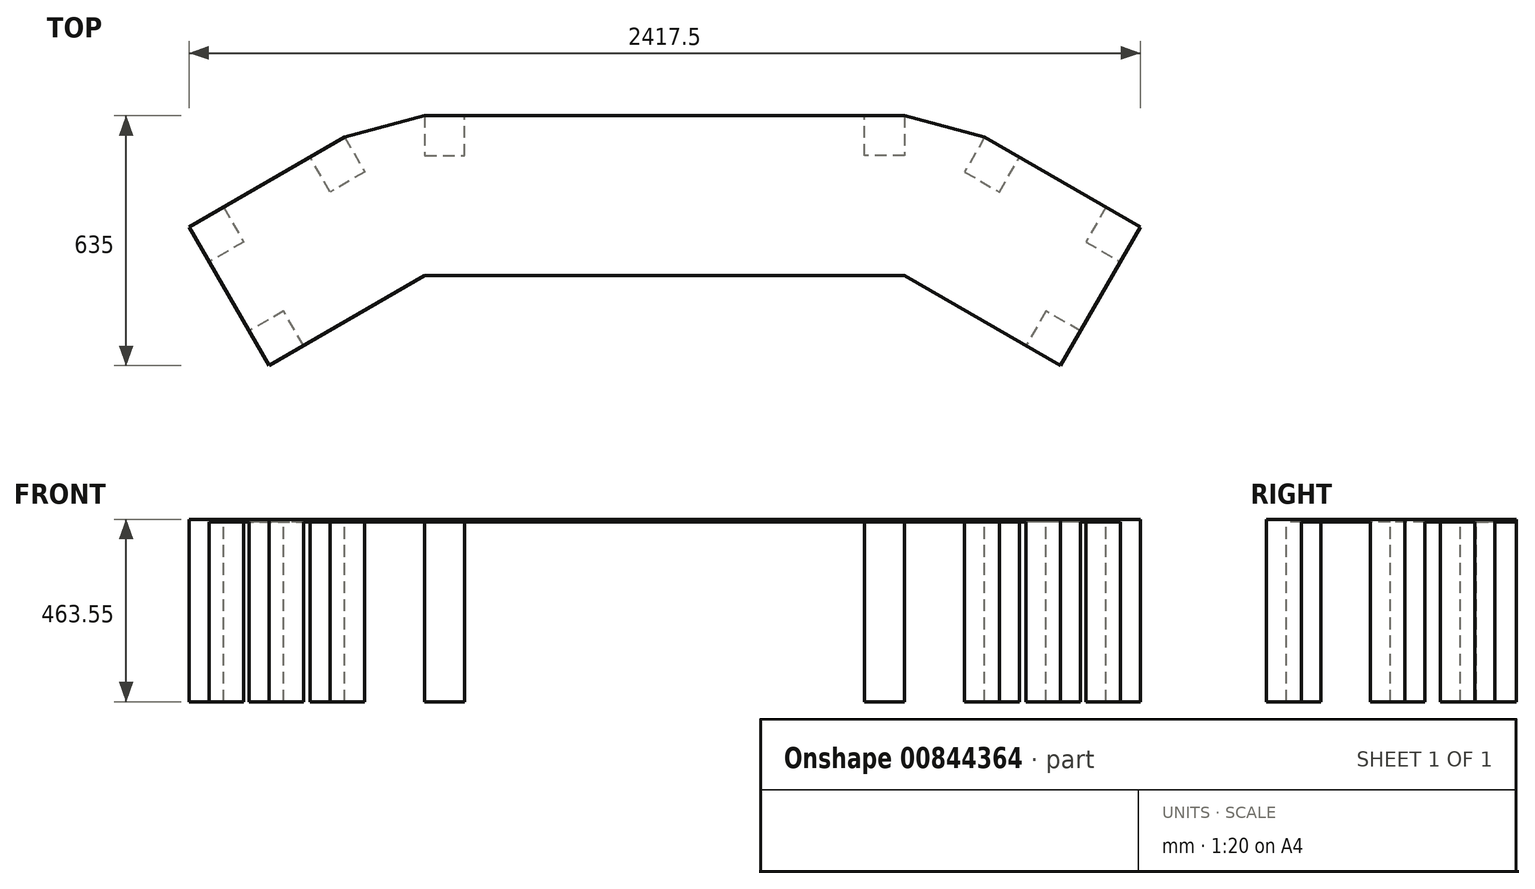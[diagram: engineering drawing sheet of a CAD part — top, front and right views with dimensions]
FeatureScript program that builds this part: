
annotation { "Feature Type Name" : "Feature", "Feature Type Description" : "" }
export const myFeature = defineFeature(function(context is Context, id is Id, definition is map)
    precondition{}
    {
        {
            var Q0;
            Q0=qCreatedBy(makeId("Top.planeOp"),FACE);
            var sketch = newSketch(context, id + "F0", { "sketchPlane" : qUnion([Q0])});
            skLineSegment(sketch, "E0.bottom", {"start": v(609.6, 203.2) * mm, "end": v(-609.6, 203.2) * mm});
            skLineSegment(sketch, "E0.top", {"start": v(609.6, -203.2) * mm, "end": v(-609.6, -203.2) * mm});
            skLineSegment(sketch, "E0.left", {"start": v(609.6, 203.2) * mm, "end": v(609.6, -203.2) * mm});
            skLineSegment(sketch, "E0.right", {"start": v(-609.6, 203.2) * mm, "end": v(-609.6, -203.2) * mm});
            skPoint(sketch, "E0.middle", {"position": v(0, 0) * mm});
            skLineSegment(sketch, "E1", {"start": v(-609.6, -203.2) * mm, "end": v(-1005.55, -431.8) * mm});
            skLineSegment(sketch, "E2", {"start": v(-1005.55, -431.8) * mm, "end": v(-1208.75, -79.85) * mm});
            skLineSegment(sketch, "E3", {"start": v(-1208.75, -79.85) * mm, "end": v(-812.8, 148.75) * mm});
            skLineSegment(sketch, "E4", {"start": v(-812.8, 148.75) * mm, "end": v(-609.6, -203.2) * mm});
            skLineSegment(sketch, "E5", {"start": v(-609.6, 203.2) * mm, "end": v(-812.8, 148.75) * mm});
            skLineSegment(sketch, "E6", {"start": v(609.6, -203.2) * mm, "end": v(1005.55, -431.8) * mm});
            skLineSegment(sketch, "E7", {"start": v(1005.55, -431.8) * mm, "end": v(1208.75, -79.85) * mm});
            skLineSegment(sketch, "E8", {"start": v(1208.75, -79.85) * mm, "end": v(812.8, 148.75) * mm});
            skLineSegment(sketch, "E9", {"start": v(812.8, 148.75) * mm, "end": v(609.6, -203.2) * mm});
            skLineSegment(sketch, "E10", {"start": v(609.6, 203.2) * mm, "end": v(812.8, 148.75) * mm});
            skSolve(sketch);
        }
        {
            var Q0;
            Q0=makeQuery(id+"F0.imprint","IMPRINT",FACE,{"disambiguationData":[TD([[makeQuery(id+"F0.imprint","IMPRINT",EDGE,{"derivedFrom":sQuery(id+"F0.wireOp",EDGE,"E6")}),1.0]])]});
            var Q1;
            Q1=makeQuery(id+"F0.imprint","IMPRINT",FACE,{"disambiguationData":[TD([[makeQuery(id+"F0.imprint","IMPRINT",EDGE,{"derivedFrom":sQuery(id+"F0.wireOp",EDGE,"E0.left")}),1.0]])]});
            var Q2;
            Q2=makeQuery(id+"F0.imprint","IMPRINT",FACE,{"disambiguationData":[TD([[makeQuery(id+"F0.imprint","IMPRINT",EDGE,{"derivedFrom":sQuery(id+"F0.wireOp",EDGE,"E0.bottom")}),1.0]])]});
            var Q3;
            Q3=makeQuery(id+"F0.imprint","IMPRINT",FACE,{"disambiguationData":[TD([[makeQuery(id+"F0.imprint","IMPRINT",EDGE,{"derivedFrom":sQuery(id+"F0.wireOp",EDGE,"E0.right")}),-1.0]])]});
            var Q4;
            Q4=makeQuery(id+"F0.imprint","IMPRINT",FACE,{"disambiguationData":[TD([[makeQuery(id+"F0.imprint","IMPRINT",EDGE,{"derivedFrom":sQuery(id+"F0.wireOp",EDGE,"E1")}),-1.0]])]});
            extrude(context, id + "F1", {"entities" : qUnion([Q0, Q1, Q2, Q3, Q4]), "depth" : 6.35 * mm, "offsetDistance" : 25.4 * mm});
        }
        {
            var Q0;
            Q0=makeQuery(id+"F1.opExtrude","CAP_FACE",FACE,{"disambiguationData":[OSD([sQuery(id+"F0.wireOp",EDGE,"E0.bottom"),sQuery(id+"F0.wireOp",EDGE,"E0.top"),sQuery(id+"F0.wireOp",EDGE,"E1"),sQuery(id+"F0.wireOp",EDGE,"E2"),sQuery(id+"F0.wireOp",EDGE,"E3"),sQuery(id+"F0.wireOp",EDGE,"E5"),sQuery(id+"F0.wireOp",EDGE,"E6"),sQuery(id+"F0.wireOp",EDGE,"E7"),sQuery(id+"F0.wireOp",EDGE,"E8"),sQuery(id+"F0.wireOp",EDGE,"E10")])],"isStart":true});
            var sketch = newSketch(context, id + "F2", { "sketchPlane" : qUnion([Q0])});
            skLineSegment(sketch, "E11", {"start": v(1208.75, 79.85) * mm, "end": v(1120.76, 29.05) * mm});
            skLineSegment(sketch, "E12", {"start": v(1120.76, 29.05) * mm, "end": v(1069.96, 117.04) * mm});
            skLineSegment(sketch, "E13", {"start": v(1069.96, 117.04) * mm, "end": v(1157.95, 167.84) * mm});
            skLineSegment(sketch, "E14", {"start": v(1157.95, 167.84) * mm, "end": v(1208.75, 79.85) * mm});
            skLineSegment(sketch, "E15", {"start": v(1005.55, 431.8) * mm, "end": v(1056.35, 343.81) * mm});
            skLineSegment(sketch, "E16", {"start": v(1056.35, 343.81) * mm, "end": v(968.36, 293.01) * mm});
            skLineSegment(sketch, "E17", {"start": v(968.36, 293.01) * mm, "end": v(917.56, 381) * mm});
            skLineSegment(sketch, "E18", {"start": v(917.56, 381) * mm, "end": v(1005.55, 431.8) * mm});
            skLineSegment(sketch, "E19", {"start": v(812.8, -148.75) * mm, "end": v(762, -60.76) * mm});
            skLineSegment(sketch, "E20", {"start": v(762, -60.76) * mm, "end": v(849.99, -9.96) * mm});
            skLineSegment(sketch, "E21", {"start": v(849.99, -9.96) * mm, "end": v(900.79, -97.95) * mm});
            skLineSegment(sketch, "E22", {"start": v(900.79, -97.95) * mm, "end": v(812.8, -148.75) * mm});
            skLineSegment(sketch, "E23", {"start": v(609.6, 203.2) * mm, "end": v(660.4, 115.21) * mm});
            skLineSegment(sketch, "E24", {"start": v(660.4, 115.21) * mm, "end": v(748.39, 166.01) * mm});
            skLineSegment(sketch, "E25", {"start": v(748.39, 166.01) * mm, "end": v(697.59, 254) * mm});
            skLineSegment(sketch, "E26", {"start": v(697.59, 254) * mm, "end": v(609.6, 203.2) * mm});
            skLineSegment(sketch, "E27", {"start": v(-1208.75, 79.85) * mm, "end": v(-1120.76, 29.05) * mm});
            skLineSegment(sketch, "E28", {"start": v(-1120.76, 29.05) * mm, "end": v(-1069.96, 117.04) * mm});
            skLineSegment(sketch, "E29", {"start": v(-1069.96, 117.04) * mm, "end": v(-1157.95, 167.84) * mm});
            skLineSegment(sketch, "E30", {"start": v(-1157.95, 167.84) * mm, "end": v(-1208.75, 79.85) * mm});
            skLineSegment(sketch, "E31", {"start": v(-1005.55, 431.8) * mm, "end": v(-917.56, 381) * mm});
            skLineSegment(sketch, "E32", {"start": v(-917.56, 381) * mm, "end": v(-968.36, 293.01) * mm});
            skLineSegment(sketch, "E33", {"start": v(-968.36, 293.01) * mm, "end": v(-1056.35, 343.81) * mm});
            skLineSegment(sketch, "E34", {"start": v(-1056.35, 343.81) * mm, "end": v(-1005.55, 431.8) * mm});
            skLineSegment(sketch, "E35", {"start": v(-609.6, 203.2) * mm, "end": v(-697.59, 254) * mm});
            skLineSegment(sketch, "E36", {"start": v(-697.59, 254) * mm, "end": v(-748.39, 166.01) * mm});
            skLineSegment(sketch, "E37", {"start": v(-748.39, 166.01) * mm, "end": v(-660.4, 115.21) * mm});
            skLineSegment(sketch, "E38", {"start": v(-660.4, 115.21) * mm, "end": v(-609.6, 203.2) * mm});
            skLineSegment(sketch, "E39", {"start": v(-812.8, -148.75) * mm, "end": v(-762, -60.76) * mm});
            skLineSegment(sketch, "E40", {"start": v(-762, -60.76) * mm, "end": v(-849.99, -9.96) * mm});
            skLineSegment(sketch, "E41", {"start": v(-849.99, -9.96) * mm, "end": v(-900.79, -97.95) * mm});
            skLineSegment(sketch, "E42", {"start": v(849.99, -9.96) * mm, "end": v(1069.96, 117.04) * mm});
            skLineSegment(sketch, "E43", {"start": v(968.36, 293.01) * mm, "end": v(1069.96, 117.04) * mm});
            skLineSegment(sketch, "E44", {"start": v(849.99, -9.96) * mm, "end": v(748.39, 166.01) * mm});
            skLineSegment(sketch, "E45", {"start": v(968.36, 293.01) * mm, "end": v(748.39, 166.01) * mm});
            skLineSegment(sketch, "E46", {"start": v(1120.76, 29.05) * mm, "end": v(900.79, -97.95) * mm});
            skLineSegment(sketch, "E47", {"start": v(762, -60.76) * mm, "end": v(660.4, 115.21) * mm});
            skLineSegment(sketch, "E48", {"start": v(697.59, 254) * mm, "end": v(917.56, 381) * mm});
            skLineSegment(sketch, "E49", {"start": v(1056.35, 343.81) * mm, "end": v(1157.95, 167.84) * mm});
            skLineSegment(sketch, "E50", {"start": v(-917.56, 381) * mm, "end": v(-697.59, 254) * mm});
            skLineSegment(sketch, "E51", {"start": v(-660.4, 115.21) * mm, "end": v(-762, -60.76) * mm});
            skLineSegment(sketch, "E52", {"start": v(-849.99, -9.96) * mm, "end": v(-1069.96, 117.04) * mm});
            skLineSegment(sketch, "E53", {"start": v(-968.36, 293.01) * mm, "end": v(-748.39, 166.01) * mm});
            skLineSegment(sketch, "E54", {"start": v(-968.36, 293.01) * mm, "end": v(-1069.96, 117.04) * mm});
            skLineSegment(sketch, "E55", {"start": v(-1056.35, 343.81) * mm, "end": v(-1157.95, 167.84) * mm});
            skLineSegment(sketch, "E56", {"start": v(-900.79, -97.95) * mm, "end": v(-1120.76, 29.05) * mm});
            skLineSegment(sketch, "E57", {"start": v(-748.39, 166.01) * mm, "end": v(-849.99, -9.96) * mm});
            skLineSegment(sketch, "E58", {"start": v(-609.6, 203.2) * mm, "end": v(-609.6, 101.6) * mm});
            skLineSegment(sketch, "E59", {"start": v(-609.6, 101.6) * mm, "end": v(-508, 101.6) * mm});
            skLineSegment(sketch, "E60", {"start": v(-508, 101.6) * mm, "end": v(-508, 203.2) * mm});
            skLineSegment(sketch, "E61", {"start": v(-508, 203.2) * mm, "end": v(-609.6, 203.2) * mm});
            skLineSegment(sketch, "E62", {"start": v(-609.6, -203.2) * mm, "end": v(-609.6, -101.6) * mm});
            skLineSegment(sketch, "E63", {"start": v(-609.6, -101.6) * mm, "end": v(-508, -101.6) * mm});
            skLineSegment(sketch, "E64", {"start": v(-508, -101.6) * mm, "end": v(-508, -203.2) * mm});
            skLineSegment(sketch, "E65", {"start": v(-508, -203.2) * mm, "end": v(-609.6, -203.2) * mm});
            skLineSegment(sketch, "E66", {"start": v(609.6, 203.2) * mm, "end": v(508, 203.2) * mm});
            skLineSegment(sketch, "E67", {"start": v(508, 203.2) * mm, "end": v(508, 101.6) * mm});
            skLineSegment(sketch, "E68", {"start": v(508, 101.6) * mm, "end": v(609.6, 101.6) * mm});
            skLineSegment(sketch, "E69", {"start": v(609.6, 101.6) * mm, "end": v(609.6, 203.2) * mm});
            skLineSegment(sketch, "E70", {"start": v(609.6, -203.2) * mm, "end": v(609.6, -101.6) * mm});
            skLineSegment(sketch, "E71", {"start": v(609.6, -101.6) * mm, "end": v(508, -101.6) * mm});
            skLineSegment(sketch, "E72", {"start": v(508, -101.6) * mm, "end": v(508, -203.2) * mm});
            skLineSegment(sketch, "E73", {"start": v(508, -203.2) * mm, "end": v(609.6, -203.2) * mm});
            skLineSegment(sketch, "E74", {"start": v(-508, 203.2) * mm, "end": v(508, 203.2) * mm});
            skLineSegment(sketch, "E75", {"start": v(609.6, 101.6) * mm, "end": v(609.6, -101.6) * mm});
            skLineSegment(sketch, "E76", {"start": v(508, -101.6) * mm, "end": v(508, 101.6) * mm});
            skLineSegment(sketch, "E77", {"start": v(-508, 101.6) * mm, "end": v(508, 101.6) * mm});
            skLineSegment(sketch, "E78", {"start": v(508, -101.6) * mm, "end": v(-508, -101.6) * mm});
            skLineSegment(sketch, "E79", {"start": v(-508, -203.2) * mm, "end": v(508, -203.2) * mm});
            skLineSegment(sketch, "E80", {"start": v(-508, 101.6) * mm, "end": v(-508, -101.6) * mm});
            skLineSegment(sketch, "E81", {"start": v(-609.6, -101.6) * mm, "end": v(-609.6, 101.6) * mm});
            skSolve(sketch);
        }
        {
            var Q0;
            Q0=makeQuery(id+"F2.imprint","IMPRINT",FACE,{"disambiguationData":[TD([[makeQuery(id+"F2.imprint","IMPRINT",EDGE,{"derivedFrom":sQuery(id+"F2.wireOp",EDGE,"E31")}),1.0]])]});
            var Q1;
            Q1=makeQuery(id+"F2.imprint","IMPRINT",FACE,{"disambiguationData":[TD([[makeQuery(id+"F2.imprint","IMPRINT",EDGE,{"derivedFrom":sQuery(id+"F2.wireOp",EDGE,"E27")}),1.0]])]});
            var Q2;
            {var subQ0=sQuery(id+"F2.wireOp",EDGE,"E39");Q2=makeQuery(id+"F2.imprint","IMPRINT",FACE,{"disambiguationData":[TD([[makeQuery(id+"F2.imprint","IMPRINT",EDGE,{"derivedFrom":subQ0}),1.0]])]});}
            var Q3;
            Q3=makeQuery(id+"F2.imprint","IMPRINT",FACE,{"disambiguationData":[TD([[makeQuery(id+"F2.imprint","IMPRINT",EDGE,{"derivedFrom":sQuery(id+"F2.wireOp",EDGE,"E62")}),-1.0]])]});
            var Q4;
            Q4=makeQuery(id+"F2.imprint","IMPRINT",FACE,{"disambiguationData":[TD([[makeQuery(id+"F2.imprint","IMPRINT",EDGE,{"derivedFrom":sQuery(id+"F2.wireOp",EDGE,"E15")}),-1.0]])]});
            var Q5;
            Q5=makeQuery(id+"F2.imprint","IMPRINT",FACE,{"disambiguationData":[TD([[makeQuery(id+"F2.imprint","IMPRINT",EDGE,{"derivedFrom":sQuery(id+"F2.wireOp",EDGE,"E11")}),-1.0]])]});
            var Q6;
            Q6=makeQuery(id+"F2.imprint","IMPRINT",FACE,{"disambiguationData":[TD([[makeQuery(id+"F2.imprint","IMPRINT",EDGE,{"derivedFrom":sQuery(id+"F2.wireOp",EDGE,"E19")}),-1.0]])]});
            var Q7;
            Q7=makeQuery(id+"F2.imprint","IMPRINT",FACE,{"disambiguationData":[TD([[makeQuery(id+"F2.imprint","IMPRINT",EDGE,{"derivedFrom":sQuery(id+"F2.wireOp",EDGE,"E70")}),1.0]])]});
            extrude(context, id + "F3", {"entities" : qUnion([Q0, Q1, Q2, Q3, Q4, Q5, Q6, Q7]), "operationType" : NewBodyOperationType.ADD, "depth" : 457.2 * mm, "offsetDistance" : 25.4 * mm});
        }
    });
